# Revit family: Electrical-Teknion-BLEPC_Power_Cube-R2018
name_source: partatom
category: Electrical Fixtures
revit_build: Autodesk Revit 2018 (Build: 20190510_1515(x64)
units: mm (PartAtom-declared; Revit-internal decimal feet)

## family parameters
Cut with Voids When Loaded = No
Host = Face
Maintain Annotation Orientation = No
OmniClass Number = 23.40.20.00
OmniClass Title = General Furniture and Specialties
Part Type = Normal
Room Calculation Point = No
Round Connector Dimension = Use Diameter
Shared = Yes

## types (3) — shared parameters
Apparent Load = 0 VA
Connector Descriptor = Power Connector
Default Elevation = 4' - 0"
Left Power Hole Depth = 0' - 0 27/32"
Manufacturer = Teknion
Manufacturer Fax = 416.661.4586
Part Number = BLEPC
Product Documentation Link = http://www.teknion.com
Product Line = Expansion Casegoods
Product Page URL = http://www.teknion.com
Series = Expansion Casegoods
Sustainability Data = http://www.teknion.com
URL = www.teknion.com
Unit Weight URL = http://www.teknion.com
Voltage = 120 V
Warranty = http://www.teknion.com

## per-type parameters (varying)
| type | Description | Has Power & Data slot | Has Power & Power slot | Has Power & USB Charger slot | Model | Right Power Hole Depth | Right Power/USB Charger |
| Power/Data, Square Grommet | Power Cube, Power/Data, Standard Solid Top Square Grommet | Yes | No | No | BLEPCDS_ | 0' - 0 9/16" | 0' - 0 9/16" |
| Power/Power, Square Grommet | Power Cube, Power/Power, Standard Solid Top Square Grommet | No | Yes | No | BLEPCPS_ | 0' - 0 27/32" | 0' - 0 9/16" |
| Power/USB Charger, Square Grommet | Power Cube, Power/USB Charger, Standard Solid Top Square Grommet | No | No | Yes | BLEPCUS_ | 0' - 0 9/16" | 0' - 0 27/32" |

## geometry (parser evidence)
native form markers: Blend x2, Sweep x2
no freeform markers — native parametric forms only
